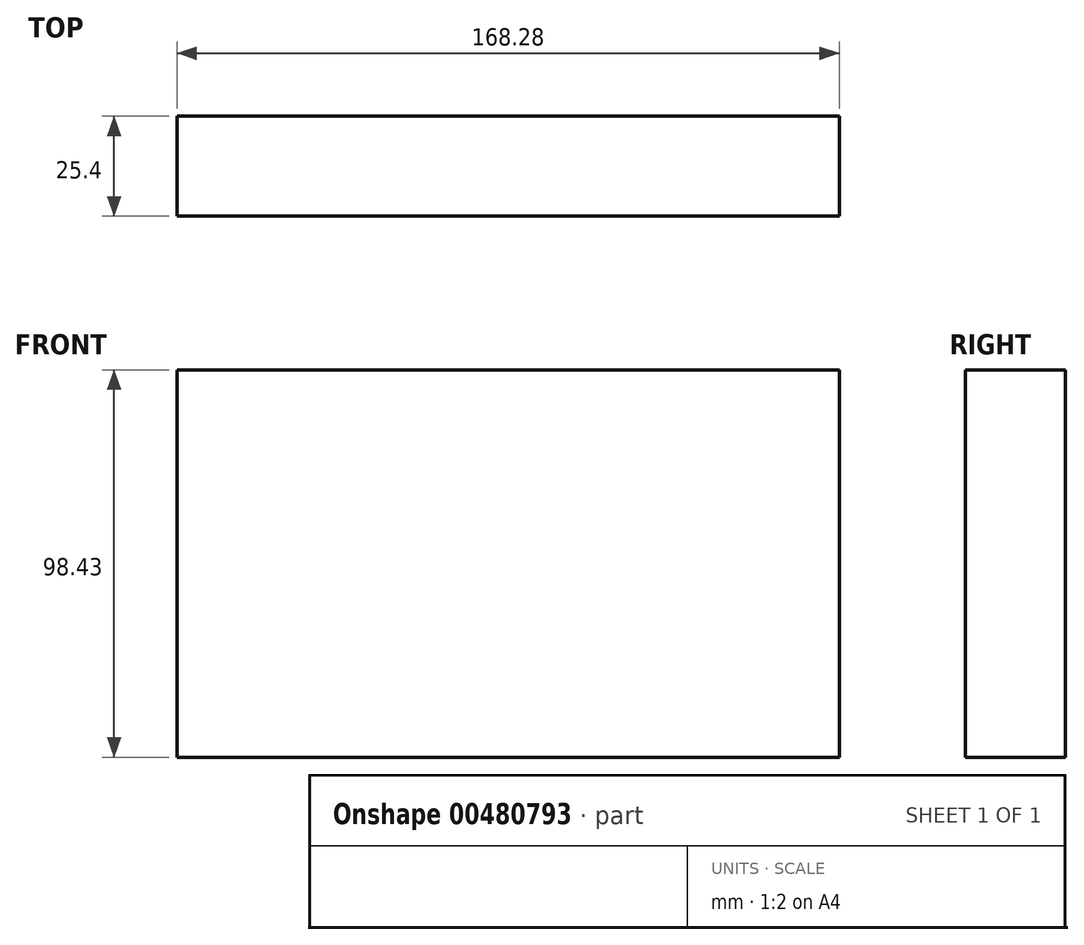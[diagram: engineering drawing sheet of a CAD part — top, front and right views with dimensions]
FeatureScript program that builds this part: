
annotation { "Feature Type Name" : "Feature", "Feature Type Description" : "" }
export const myFeature = defineFeature(function(context is Context, id is Id, definition is map)
    precondition{}
    {
        {
            var Q0;
            Q0=qCreatedBy(makeId("Front.planeOp"),FACE);
            var sketch = newSketch(context, id + "F0", { "sketchPlane" : qUnion([Q0])});
            skLineSegment(sketch, "E0.bottom", {"start": v(-41.99, -25.83) * mm, "end": v(126.29, -25.83) * mm});
            skLineSegment(sketch, "E0.top", {"start": v(-41.99, 72.6) * mm, "end": v(126.29, 72.6) * mm});
            skLineSegment(sketch, "E0.left", {"start": v(-41.99, -25.83) * mm, "end": v(-41.99, 72.6) * mm});
            skLineSegment(sketch, "E0.right", {"start": v(126.29, -25.83) * mm, "end": v(126.29, 72.6) * mm});
            skLineSegment(sketch, "E1", {"start": v(34.21, 72.6) * mm, "end": v(34.21, -25.83) * mm});
            skSolve(sketch);
        }
        {
            var Q0;
            {var subQ0=sQuery(id+"F0.wireOp",EDGE,"E0.left");Q0=makeQuery(id+"F0.imprint","IMPRINT",FACE,{"disambiguationData":[TD([[makeQuery(id+"F0.imprint","IMPRINT",EDGE,{"derivedFrom":subQ0}),-1.0]])]});}
            var Q1;
            {var subQ0=sQuery(id+"F0.wireOp",EDGE,"E0.right");Q1=makeQuery(id+"F0.imprint","IMPRINT",FACE,{"disambiguationData":[TD([[makeQuery(id+"F0.imprint","IMPRINT",EDGE,{"derivedFrom":subQ0}),1.0]])]});}
            extrude(context, id + "F1", {"entities" : qUnion([Q0, Q1]), "depth" : 25.4 * mm});
        }
    });
